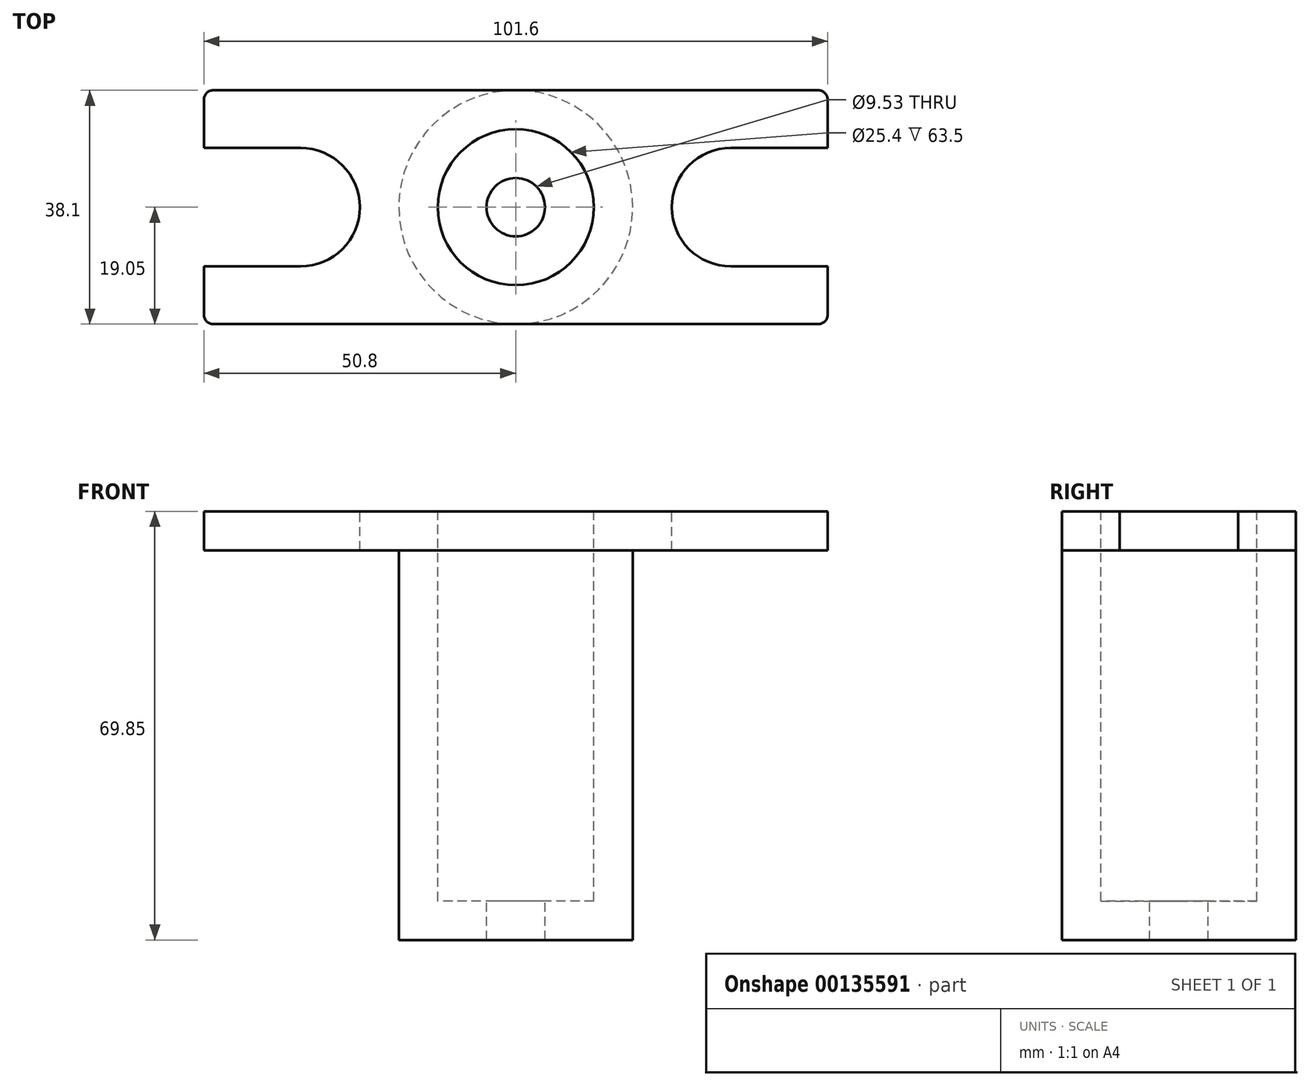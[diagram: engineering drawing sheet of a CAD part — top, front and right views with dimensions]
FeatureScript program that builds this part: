
annotation { "Feature Type Name" : "Feature", "Feature Type Description" : "" }
export const myFeature = defineFeature(function(context is Context, id is Id, definition is map)
    precondition{}
    {
        {
            var Q0;
            Q0=qCreatedBy(makeId("Front.planeOp"),FACE);
            var sketch = newSketch(context, id + "F0", { "sketchPlane" : qUnion([Q0])});
            skLineSegment(sketch, "E0", {"start": v(0, 87.06) * mm, "end": v(0, 0) * mm, "construction": true});
            skLineSegment(sketch, "E1", {"start": v(0, 0) * mm, "end": v(-4.76, 0) * mm});
            skLineSegment(sketch, "E2", {"start": v(-4.76, 0) * mm, "end": v(-19.05, 0) * mm});
            skLineSegment(sketch, "E3", {"start": v(-19.05, 0) * mm, "end": v(-19.05, 63.5) * mm});
            skLineSegment(sketch, "E4", {"start": v(-19.05, 63.5) * mm, "end": v(-50.8, 63.5) * mm});
            skLineSegment(sketch, "E5", {"start": v(-50.8, 63.5) * mm, "end": v(-50.8, 69.85) * mm});
            skLineSegment(sketch, "E6", {"start": v(-12.7, 69.85) * mm, "end": v(0, 69.85) * mm});
            skLineSegment(sketch, "E7", {"start": v(-4.76, 0) * mm, "end": v(-4.76, 6.35) * mm});
            skLineSegment(sketch, "E8", {"start": v(-4.76, 6.35) * mm, "end": v(0, 6.35) * mm});
            skLineSegment(sketch, "E9", {"start": v(-12.7, 6.35) * mm, "end": v(-4.76, 6.35) * mm});
            skLineSegment(sketch, "E10", {"start": v(-12.7, 69.85) * mm, "end": v(-12.7, 6.35) * mm});
            skLineSegment(sketch, "E11", {"start": v(-50.8, 69.85) * mm, "end": v(-12.7, 69.85) * mm});
            skSolve(sketch);
        }
        {
            var Q0;
            Q0 = qSketchRegion(id + "F0", true);
            var Q1;
            Q1 = qSketchRegion(id + "F2", true);
            var Q2;
            Q2=sQuery(id+"F0.wireOp",EDGE,"E0");
            revolve(context, id + "F1", {"entities" : qUnion([Q0, Q1]), "axis" : qUnion([Q2]), "revolveType" : RevolveType.FULL});
        }
        {
            var Q0;
            Q0=makeQuery(id+"F1.opRevolve","SWEPT_FACE",FACE,{"disambiguationData":[OSD([sQuery(id+"F0.wireOp",EDGE,"E11")])]});
            var sketch = newSketch(context, id + "F2", { "sketchPlane" : qUnion([Q0])});
            skLineSegment(sketch, "E12", {"start": v(-50.8, 0) * mm, "end": v(50.8, 0) * mm, "construction": true});
            skLineSegment(sketch, "E13", {"start": v(-50.8, 9.65) * mm, "end": v(-35.05, 9.65) * mm});
            skLineSegment(sketch, "E14", {"start": v(-50.8, -9.65) * mm, "end": v(-35.05, -9.65) * mm});
            skLineSegment(sketch, "E15", {"start": v(50.8, 9.65) * mm, "end": v(35.05, 9.65) * mm});
            skLineSegment(sketch, "E16", {"start": v(50.8, -9.65) * mm, "end": v(35.05, -9.65) * mm});
            skLineSegment(sketch, "E17", {"start": v(-50.8, 9.65) * mm, "end": v(-50.8, 17.53) * mm});
            skLineSegment(sketch, "E18", {"start": v(-49.28, 19.05) * mm, "end": v(49.28, 19.05) * mm});
            skLineSegment(sketch, "E19", {"start": v(50.8, 9.65) * mm, "end": v(50.8, 17.53) * mm});
            skLineSegment(sketch, "E20", {"start": v(50.8, -9.65) * mm, "end": v(50.8, -17.53) * mm});
            skLineSegment(sketch, "E21", {"start": v(49.28, -19.05) * mm, "end": v(-49.28, -19.05) * mm});
            skArc(sketch, "E22", {"start": v(-49.28, 19.05) * mm, "mid": v(-50.35, 18.6) * mm, "end": v(-50.8, 17.53) * mm});
            skLineSegment(sketch, "E23", {"start": v(-50.8, -9.65) * mm, "end": v(-50.8, -17.53) * mm});
            skArc(sketch, "E24", {"start": v(-50.8, -17.53) * mm, "mid": v(-50.35, -18.6) * mm, "end": v(-49.28, -19.05) * mm});
            skArc(sketch, "E25", {"start": v(49.28, -19.05) * mm, "mid": v(50.35, -18.6) * mm, "end": v(50.8, -17.53) * mm});
            skArc(sketch, "E26", {"start": v(50.8, 17.53) * mm, "mid": v(50.35, 18.6) * mm, "end": v(49.28, 19.05) * mm});
            skArc(sketch, "E27", {"start": v(-35.05, -9.65) * mm, "mid": v(-25.4, 0) * mm, "end": v(-35.05, 9.65) * mm});
            skArc(sketch, "E28", {"start": v(35.05, 9.65) * mm, "mid": v(25.4, 0) * mm, "end": v(35.05, -9.65) * mm});
            skCircle(sketch, "E29.0", {"center": v(0, 0) * mm, "radius": 50.8 * mm});
            skLineSegment(sketch, "E30", {"start": v(0, 0) * mm, "end": v(0, 50.8) * mm, "construction": true});
            skLineSegment(sketch, "E31", {"start": v(0, 0) * mm, "end": v(0, -50.8) * mm, "construction": true});
            skCircle(sketch, "E32.0", {"center": v(0, 0) * mm, "radius": 12.7 * mm});
            skSolve(sketch);
        }
        {
            var Q0;
            {var subQ0=sQuery(id+"F2.wireOp",EDGE,"E29.0");var subQ1=sQuery(id+"F2.wireOp",EDGE,"E18");var subQ2=makeQuery(id+"F2.imprint","INTERSECT",VERTEX,{"disambiguationData":[OD(0.0)],"derivedFrom":[subQ1,subQ0]});Q0=makeQuery(id+"F2.imprint","IMPRINT",FACE,{"disambiguationData":[TD([[makeQuery(id+"F2.imprint","IMPRINT",EDGE,{"disambiguationData":[TD([[subQ2,-1.0]])],"derivedFrom":subQ1}),1.0]])]});}
            var Q1;
            {var subQ0=sQuery(id+"F2.wireOp",EDGE,"E29.0");var subQ1=sQuery(id+"F2.wireOp",EDGE,"E21");var subQ2=makeQuery(id+"F2.imprint","INTERSECT",VERTEX,{"disambiguationData":[OD(0.0)],"derivedFrom":[subQ1,subQ0]});Q1=makeQuery(id+"F2.imprint","IMPRINT",FACE,{"disambiguationData":[TD([[makeQuery(id+"F2.imprint","IMPRINT",EDGE,{"disambiguationData":[TD([[subQ2,-1.0]])],"derivedFrom":subQ1}),1.0]])]});}
            var Q2;
            {var subQ0=sQuery(id+"F2.wireOp",EDGE,"E27");Q2=makeQuery(id+"F2.imprint","IMPRINT",FACE,{"disambiguationData":[TD([[makeQuery(id+"F2.imprint","IMPRINT",EDGE,{"derivedFrom":subQ0}),1.0]])]});}
            var Q3;
            {var subQ0=sQuery(id+"F2.wireOp",EDGE,"E28");Q3=makeQuery(id+"F2.imprint","IMPRINT",FACE,{"disambiguationData":[TD([[makeQuery(id+"F2.imprint","IMPRINT",EDGE,{"derivedFrom":subQ0}),1.0]])]});}
            extrude(context, id + "F3", {"entities" : qUnion([Q0, Q1, Q2, Q3]), "operationType" : NewBodyOperationType.REMOVE, "endBound" : BoundingType.THROUGH_ALL, "oppositeDirection" : true, "depth" : 25.4 * mm});
        }
        {
            var Q0;
            {var subQ4=sQuery(id+"F2.wireOp",EDGE,"E17");Q0=makeQuery(id+"F2.imprint","IMPRINT",FACE,{"disambiguationData":[TD([[makeQuery(id+"F2.imprint","IMPRINT",EDGE,{"derivedFrom":subQ4}),-1.0]])]});}
            var Q1;
            {var subQ1=sQuery(id+"F2.wireOp",EDGE,"E23");Q1=makeQuery(id+"F2.imprint","IMPRINT",FACE,{"disambiguationData":[TD([[makeQuery(id+"F2.imprint","IMPRINT",EDGE,{"derivedFrom":subQ1}),1.0]])]});}
            var Q2;
            {var subQ4=sQuery(id+"F2.wireOp",EDGE,"E19");Q2=makeQuery(id+"F2.imprint","IMPRINT",FACE,{"disambiguationData":[TD([[makeQuery(id+"F2.imprint","IMPRINT",EDGE,{"derivedFrom":subQ4}),1.0]])]});}
            var Q3;
            {var subQ4=sQuery(id+"F2.wireOp",EDGE,"E20");Q3=makeQuery(id+"F2.imprint","IMPRINT",FACE,{"disambiguationData":[TD([[makeQuery(id+"F2.imprint","IMPRINT",EDGE,{"derivedFrom":subQ4}),-1.0]])]});}
            extrude(context, id + "F4", {"entities" : qUnion([Q0, Q1, Q2, Q3]), "operationType" : NewBodyOperationType.ADD, "oppositeDirection" : true, "depth" : 6.35 * mm});
        }
    });
